# Revit family: PT, PS, 66, 96, 69, 612
name_source: partatom
category: Windows
revit_build: Autodesk Revit LT 2016 (Build: 20150220_1215(x64)
units: mm (PartAtom-declared; Revit-internal decimal feet)

## family parameters
Always vertical = Yes
Cut with Voids When Loaded = No
Host = Wall
OmniClass Number = 23.30.20.00
OmniClass Title = Windows
Room Calculation Point = No
Shared = No

## types (4) — shared parameters
Aluminium anodized = Aluminium
Default Sill Height = 914 mm
Glazing = Glass
Manufacturer = Robmeg
Plaster = 5 mm  [stored 0.0164042 ft]
Rough Height = 1219 mm
URL = http://www.robmeg.co.za
Wall Closure = By host

## per-type parameters (varying)
| type | Description | Height | Model | Side hung | Top hung | Width |
| PT Type- 66 | Anodized Aluminium | 610 mm  [stored 2.00131 ft] | PT 66 | No | Yes | 610 mm  [stored 2.00131 ft] |
| PS Type- 69 | Anodized Aluminium | 910 mm  [stored 2.98556 ft] | PS 69 | Yes | No | 610 mm  [stored 2.00131 ft] |
| PS type- 612 | Anodized Aluminium | 1210 mm  [stored 3.96982 ft] | PS 612 | Yes | No | 610 mm  [stored 2.00131 ft] |
| PT Type- 96 | Anodized Alumium | 610 mm  [stored 2.00131 ft] | PT 96 | No | Yes | 910 mm  [stored 2.98556 ft] |

note: [stored X ft] marks values corroborated as IEEE doubles in the binary element streams (Revit-internal decimal feet)

## geometry (parser evidence)
native form markers: Sweep x4
no freeform markers — native parametric forms only
